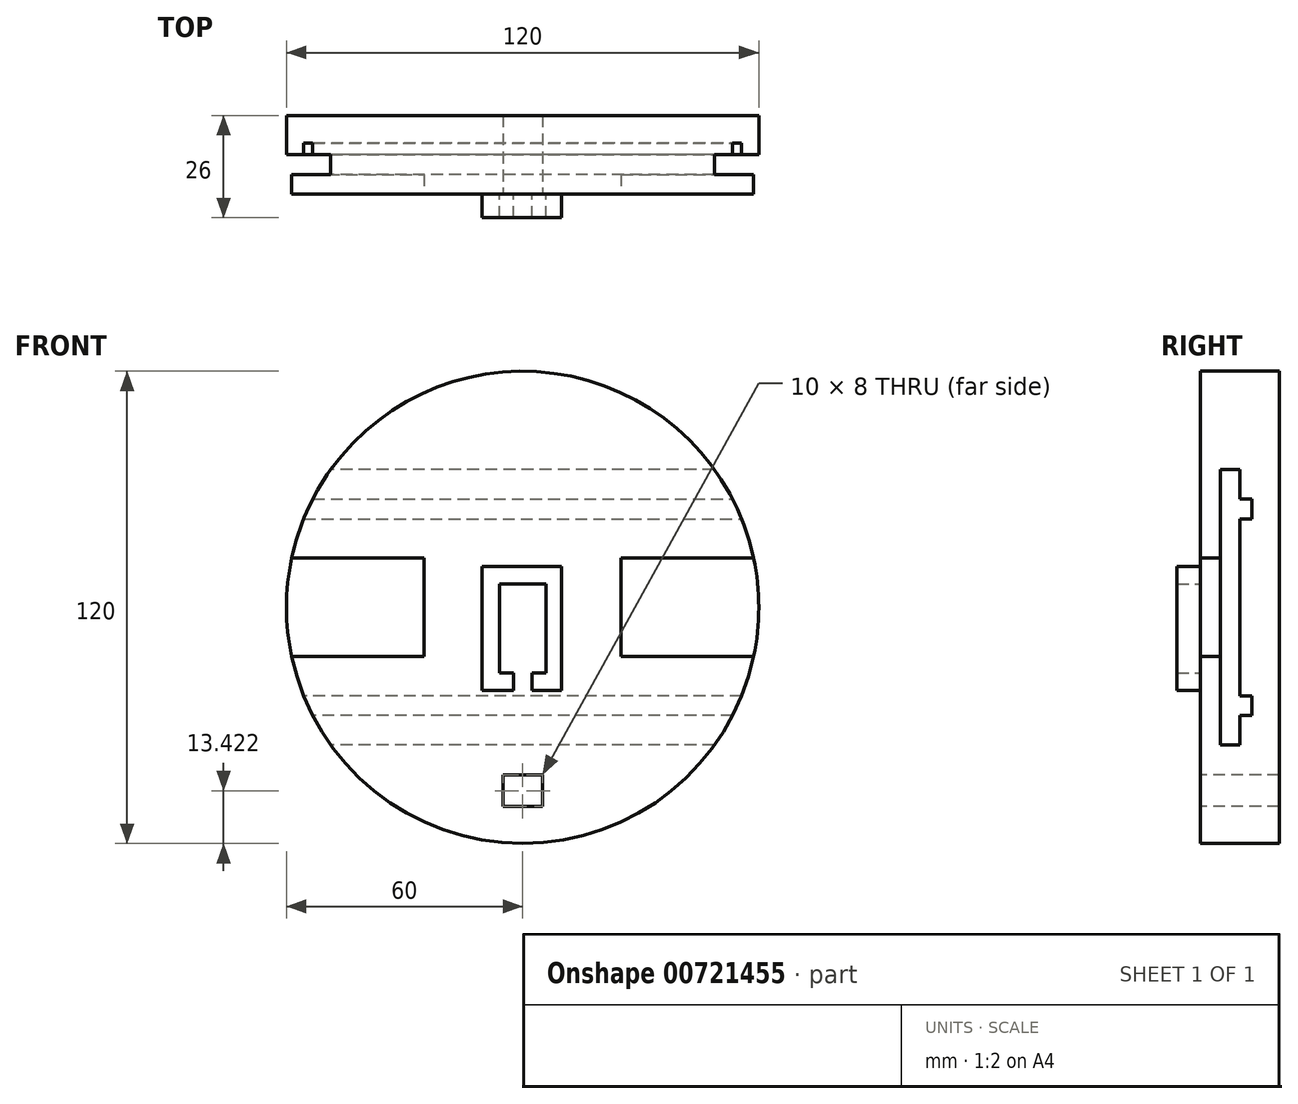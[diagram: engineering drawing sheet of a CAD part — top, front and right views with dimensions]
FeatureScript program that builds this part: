
annotation { "Feature Type Name" : "Feature", "Feature Type Description" : "" }
export const myFeature = defineFeature(function(context is Context, id is Id, definition is map)
    precondition{}
    {
        {
            var Q0;
            Q0=qCreatedBy(makeId("Front.planeOp"),FACE);
            var sketch = newSketch(context, id + "F0", { "sketchPlane" : qUnion([Q0])});
            skCircle(sketch, "E0", {"center": v(0, 0) * mm, "radius": 60 * mm});
            skSolve(sketch);
        }
        {
            var Q0;
            Q0=makeQuery(id+"F0.imprint","IMPRINT",FACE,{"disambiguationData":[TD([[makeQuery(id+"F0.imprint","IMPRINT",EDGE,{"derivedFrom":sQuery(id+"F0.wireOp",EDGE,"E0")}),1.0]])]});
            extrude(context, id + "F1", {"entities" : qUnion([Q0]), "depth" : 20 * mm, "offsetDistance" : 25.4 * mm});
        }
        {
            var Q0;
            Q0=makeQuery(id+"F1.opExtrude","CAP_FACE",FACE,{"disambiguationData":[OSD([sQuery(id+"F0.wireOp",EDGE,"E0")])],"isStart":false});
            var sketch = newSketch(context, id + "F2", { "sketchPlane" : qUnion([Q0])});
            skLineSegment(sketch, "E1.bottom", {"start": v(-60, 12.5) * mm, "end": v(60, 12.5) * mm});
            skLineSegment(sketch, "E1.top", {"start": v(-60, -12.5) * mm, "end": v(60, -12.5) * mm});
            skLineSegment(sketch, "E1.left", {"start": v(-60, 12.5) * mm, "end": v(-60, -12.5) * mm});
            skLineSegment(sketch, "E1.right", {"start": v(60, 12.5) * mm, "end": v(60, -12.5) * mm});
            skPoint(sketch, "E1.middle", {"position": v(0, 0) * mm});
            skLineSegment(sketch, "E2", {"start": v(-25, 12.5) * mm, "end": v(-25, -12.5) * mm});
            skLineSegment(sketch, "E3", {"start": v(25, 12.5) * mm, "end": v(25, -12.5) * mm});
            skSolve(sketch);
        }
        {
            var Q0;
            {var subQ4=sQuery(id+"F2.wireOp",EDGE,"E2");Q0=makeQuery(id+"F2.imprint","IMPRINT",FACE,{"disambiguationData":[TD([[makeQuery(id+"F2.imprint","IMPRINT",EDGE,{"derivedFrom":subQ4}),-1.0]])]});}
            var Q1;
            {var subQ4=sQuery(id+"F2.wireOp",EDGE,"E3");Q1=makeQuery(id+"F2.imprint","IMPRINT",FACE,{"disambiguationData":[TD([[makeQuery(id+"F2.imprint","IMPRINT",EDGE,{"derivedFrom":subQ4}),1.0]])]});}
            extrude(context, id + "F3", {"entities" : qUnion([Q0, Q1]), "operationType" : NewBodyOperationType.REMOVE, "oppositeDirection" : true, "depth" : 10 * mm, "offsetDistance" : 25.4 * mm});
        }
        {
            var Q0;
            Q0=qCreatedBy(makeId("Right.planeOp"),FACE);
            var sketch = newSketch(context, id + "F4", { "sketchPlane" : qUnion([Q0])});
            skPoint(sketch, "E4.middle", {"position": v(0, 0) * mm});
            skLineSegment(sketch, "E5.bottom", {"start": v(-10, 35) * mm, "end": v(-15, 35) * mm});
            skLineSegment(sketch, "E5.top", {"start": v(-10, -35) * mm, "end": v(-15, -35) * mm});
            skLineSegment(sketch, "E5.left", {"start": v(-10, 35) * mm, "end": v(-10, -35) * mm});
            skLineSegment(sketch, "E5.right", {"start": v(-15, 35) * mm, "end": v(-15, -35) * mm});
            skSolve(sketch);
        }
        {
            var Q0;
            Q0=qSketchRegion(id+"F4",true);
            extrude(context, id + "F5", {"entities" : qUnion([Q0]), "operationType" : NewBodyOperationType.REMOVE, "endBound" : BoundingType.SYMMETRIC, "depth" : 120 * mm, "offsetDistance" : 25.4 * mm});
        }
        {
            var Q0;
            {var subQ0=sQuery(id+"F2.wireOp",EDGE,"E1.top");var subQ1=sQuery(id+"F2.wireOp",EDGE,"E1.bottom");var subQ2=sQuery(id+"F0.wireOp",EDGE,"E0");Q0=makeQuery(id+"F5.boolean.opBoolean","MERGE",FACE,{"derivedFrom":[makeQuery(id+"F3.boolean.opBoolean","COPY",FACE,{"derivedFrom":makeQuery(id+"F3.opExtrude","CAP_FACE",FACE,{"disambiguationData":[OSD([subQ2,subQ1,subQ0,sQuery(id+"F2.wireOp",EDGE,"E2")])],"isStart":false})}),makeQuery(id+"F3.boolean.opBoolean","COPY",FACE,{"derivedFrom":makeQuery(id+"F3.opExtrude","CAP_FACE",FACE,{"disambiguationData":[OSD([subQ2,subQ1,subQ0,sQuery(id+"F2.wireOp",EDGE,"E3")])],"isStart":false})}),makeQuery(id+"F5.opExtrude","SWEPT_FACE",FACE,{"disambiguationData":[OSD([sQuery(id+"F4.wireOp",EDGE,"E5.left")])]})]});}
            var sketch = newSketch(context, id + "F6", { "sketchPlane" : qUnion([Q0])});
            skLineSegment(sketch, "E6.bottom", {"start": v(30, -25) * mm, "end": v(-30, -25) * mm});
            skLineSegment(sketch, "E6.top", {"start": v(30, 25) * mm, "end": v(-30, 25) * mm});
            skLineSegment(sketch, "E6.left", {"start": v(30, -25) * mm, "end": v(30, 25) * mm});
            skLineSegment(sketch, "E6.right", {"start": v(-30, -25) * mm, "end": v(-30, 25) * mm});
            skPoint(sketch, "E6.middle", {"position": v(0, 0) * mm});
            skLineSegment(sketch, "E7.bottom", {"start": v(0, 27.5) * mm, "end": v(-60, 27.5) * mm});
            skLineSegment(sketch, "E7.top", {"start": v(0, 22.5) * mm, "end": v(-60, 22.5) * mm});
            skLineSegment(sketch, "E7.right", {"start": v(-60, 27.5) * mm, "end": v(-60, 22.5) * mm});
            skPoint(sketch, "E7.middle", {"position": v(-30, 25) * mm});
            skLineSegment(sketch, "E8.bottom", {"start": v(0, -22.5) * mm, "end": v(-60, -22.5) * mm});
            skLineSegment(sketch, "E8.top", {"start": v(0, -27.5) * mm, "end": v(-60, -27.5) * mm});
            skLineSegment(sketch, "E8.right", {"start": v(-60, -22.5) * mm, "end": v(-60, -27.5) * mm});
            skPoint(sketch, "E8.middle", {"position": v(-30, -25) * mm});
            skLineSegment(sketch, "E9.bottom", {"start": v(0, 22.5) * mm, "end": v(60, 22.5) * mm});
            skLineSegment(sketch, "E9.top", {"start": v(0, 27.5) * mm, "end": v(60, 27.5) * mm});
            skLineSegment(sketch, "E9.right", {"start": v(60, 22.5) * mm, "end": v(60, 27.5) * mm});
            skPoint(sketch, "E9.middle", {"position": v(30, 25) * mm});
            skLineSegment(sketch, "E10.bottom", {"start": v(0, -22.5) * mm, "end": v(60, -22.5) * mm});
            skLineSegment(sketch, "E10.top", {"start": v(0, -27.5) * mm, "end": v(60, -27.5) * mm});
            skLineSegment(sketch, "E10.right", {"start": v(60, -22.5) * mm, "end": v(60, -27.5) * mm});
            skPoint(sketch, "E10.middle", {"position": v(30, -25) * mm});
            skSolve(sketch);
        }
        {
            var Q0;
            {var subQ1=sQuery(id+"F6.wireOp",EDGE,"E6.bottom");Q0=makeQuery(id+"F6.imprint","IMPRINT",FACE,{"disambiguationData":[TD([[makeQuery(id+"F6.imprint","IMPRINT",EDGE,{"derivedFrom":subQ1}),1.0]])]});}
            var Q1;
            {var subQ8=sQuery(id+"F6.wireOp",EDGE,"E6.top");Q1=makeQuery(id+"F6.imprint","IMPRINT",FACE,{"disambiguationData":[TD([[makeQuery(id+"F6.imprint","IMPRINT",EDGE,{"derivedFrom":subQ8}),-1.0]])]});}
            var Q2;
            {var subQ5=sQuery(id+"F6.wireOp",EDGE,"E6.top");Q2=makeQuery(id+"F6.imprint","IMPRINT",FACE,{"disambiguationData":[TD([[makeQuery(id+"F6.imprint","IMPRINT",EDGE,{"derivedFrom":subQ5}),1.0]])]});}
            var Q3;
            {var subQ6=sQuery(id+"F6.wireOp",EDGE,"E6.bottom");Q3=makeQuery(id+"F6.imprint","IMPRINT",FACE,{"disambiguationData":[TD([[makeQuery(id+"F6.imprint","IMPRINT",EDGE,{"derivedFrom":subQ6}),-1.0]])]});}
            extrude(context, id + "F7", {"entities" : qUnion([Q0, Q1, Q2, Q3]), "operationType" : NewBodyOperationType.REMOVE, "oppositeDirection" : true, "depth" : 3 * mm, "offsetDistance" : 25.4 * mm});
        }
        {
            var Q0;
            Q0=makeQuery(id+"F1.opExtrude","CAP_FACE",FACE,{"disambiguationData":[OSD([sQuery(id+"F0.wireOp",EDGE,"E0")])],"isStart":false});
            var sketch = newSketch(context, id + "F8", { "sketchPlane" : qUnion([Q0])});
            skPoint(sketch, "E11.middle", {"position": v(0, 0) * mm});
            skPoint(sketch, "E12.oppositeSnap0", {"position": v(5.9, 0) * mm});
            skLineSegment(sketch, "E12.bottom", {"start": v(-5.9, 5.9) * mm, "end": v(5.9, 5.9) * mm});
            skLineSegment(sketch, "E12.top", {"start": v(-5.9, -16.6) * mm, "end": v(5.9, -16.6) * mm});
            skLineSegment(sketch, "E12.left", {"start": v(-5.9, 5.9) * mm, "end": v(-5.9, -16.6) * mm});
            skLineSegment(sketch, "E12.right", {"start": v(5.9, 5.9) * mm, "end": v(5.9, -16.6) * mm});
            skLineSegment(sketch, "E13.bottom", {"start": v(5.9, 5.9) * mm, "end": v(-10.26, 5.9) * mm});
            skLineSegment(sketch, "E13.top", {"start": v(5.9, -21.15) * mm, "end": v(-10.26, -21.15) * mm});
            skLineSegment(sketch, "E13.left", {"start": v(5.9, 5.9) * mm, "end": v(5.9, -21.15) * mm});
            skLineSegment(sketch, "E13.right", {"start": v(-10.26, 5.9) * mm, "end": v(-10.26, -21.15) * mm});
            skLineSegment(sketch, "E14.bottom", {"start": v(-10.26, -21.15) * mm, "end": v(9.94, -21.15) * mm});
            skLineSegment(sketch, "E14.top", {"start": v(-10.26, 10.42) * mm, "end": v(9.94, 10.42) * mm});
            skLineSegment(sketch, "E14.left", {"start": v(-10.26, -21.15) * mm, "end": v(-10.26, 10.42) * mm});
            skLineSegment(sketch, "E14.right", {"start": v(9.94, -21.15) * mm, "end": v(9.94, 10.42) * mm});
            skLineSegment(sketch, "E15.bottom", {"start": v(2.35, -21.15) * mm, "end": v(-2.35, -21.15) * mm});
            skLineSegment(sketch, "E15.top", {"start": v(2.35, -12.05) * mm, "end": v(-2.35, -12.05) * mm});
            skLineSegment(sketch, "E15.left", {"start": v(2.35, -21.15) * mm, "end": v(2.35, -12.05) * mm});
            skLineSegment(sketch, "E15.right", {"start": v(-2.35, -21.15) * mm, "end": v(-2.35, -12.05) * mm});
            skPoint(sketch, "E15.middle", {"position": v(0, -16.6) * mm});
            skSolve(sketch);
        }
        {
            var Q0;
            {var subQ7=sQuery(id+"F8.wireOp",EDGE,"E12.left");Q0=makeQuery(id+"F8.imprint","IMPRINT",FACE,{"disambiguationData":[TD([[makeQuery(id+"F8.imprint","IMPRINT",EDGE,{"derivedFrom":subQ7}),-1.0]])]});}
            var Q1;
            {var subQ10=sQuery(id+"F8.wireOp",EDGE,"E14.top");Q1=makeQuery(id+"F8.imprint","IMPRINT",FACE,{"disambiguationData":[TD([[makeQuery(id+"F8.imprint","IMPRINT",EDGE,{"derivedFrom":subQ10}),-1.0]])]});}
            var Q2;
            {var subQ0=sQuery(id+"F8.wireOp",EDGE,"E13.left");var subQ1=sQuery(id+"F8.wireOp",EDGE,"E12.top");var subQ2=makeQuery(id+"F8.imprint","INTERSECT",VERTEX,{"derivedFrom":[subQ1,subQ0]});Q2=makeQuery(id+"F8.imprint","IMPRINT",FACE,{"disambiguationData":[TD([[makeQuery(id+"F8.imprint","IMPRINT",EDGE,{"disambiguationData":[TD([[subQ2,1.0]])],"derivedFrom":subQ1}),-1.0]])]});}
            extrude(context, id + "F9", {"entities" : qUnion([Q0, Q1, Q2]), "operationType" : NewBodyOperationType.ADD, "depth" : 6 * mm, "offsetDistance" : 25.4 * mm});
        }
        {
            var Q0;
            Q0=makeQuery(id+"F1.opExtrude","CAP_FACE",FACE,{"disambiguationData":[OSD([sQuery(id+"F0.wireOp",EDGE,"E0")])],"isStart":false});
            var sketch = newSketch(context, id + "F10", { "sketchPlane" : qUnion([Q0])});
            skLineSegment(sketch, "E16.bottom", {"start": v(-5, -42.58) * mm, "end": v(5, -42.58) * mm});
            skLineSegment(sketch, "E16.top", {"start": v(-5, -50.58) * mm, "end": v(5, -50.58) * mm});
            skLineSegment(sketch, "E16.left", {"start": v(-5, -42.58) * mm, "end": v(-5, -50.58) * mm});
            skLineSegment(sketch, "E16.right", {"start": v(5, -42.58) * mm, "end": v(5, -50.58) * mm});
            skSolve(sketch);
        }
        {
            var Q0;
            Q0=makeQuery(id+"F10.imprint","IMPRINT",FACE,{"disambiguationData":[TD([[makeQuery(id+"F10.imprint","IMPRINT",EDGE,{"derivedFrom":sQuery(id+"F10.wireOp",EDGE,"E16.bottom")}),-1.0]])]});
            extrude(context, id + "F11", {"entities" : qUnion([Q0]), "operationType" : NewBodyOperationType.REMOVE, "endBound" : BoundingType.THROUGH_ALL, "oppositeDirection" : true, "depth" : 25.4 * mm, "offsetDistance" : 25.4 * mm});
        }
    });
